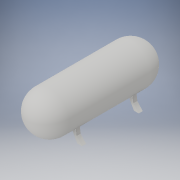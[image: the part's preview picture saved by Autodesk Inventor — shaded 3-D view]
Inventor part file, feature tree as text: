
AUTODESK INVENTOR PART (.ipt)
format: ipt  version: 2017 (Build 210142000, 142)  size: 147,968 bytes
history: native  units: mm
features: mirror x3, sketch x2, other x1, revolve x1, plane x1, extrude x1, projected_geometry x1
ambient origin geometry x8: Origin, YZ Plane, XZ Plane, XY Plane, X Axis, Y Axis, Z Axis, Center Point
bodies: Body1 (feature_tree)
feature tree (10):
  other  "Gascontainer"
  revolve  "Umdrehung1"
  mirror  "Spiegeln1"
  plane  "Arbeitsebene1"
  extrude  "Extrusion2"  Depth=1000.0mm
  mirror  "Spiegeln2"
  mirror  "Spiegeln3"
  sketch  "Skizze3"  dims[d5=13.962634mm d6=1000.0mm]
  sketch  "Skizze4"  dims[d7=500.0mm d8=-750.0mm d9=600.0mm d10=100.0mm d11=0.0mm]
  projected_geometry  "Projizierte Kontur2"
